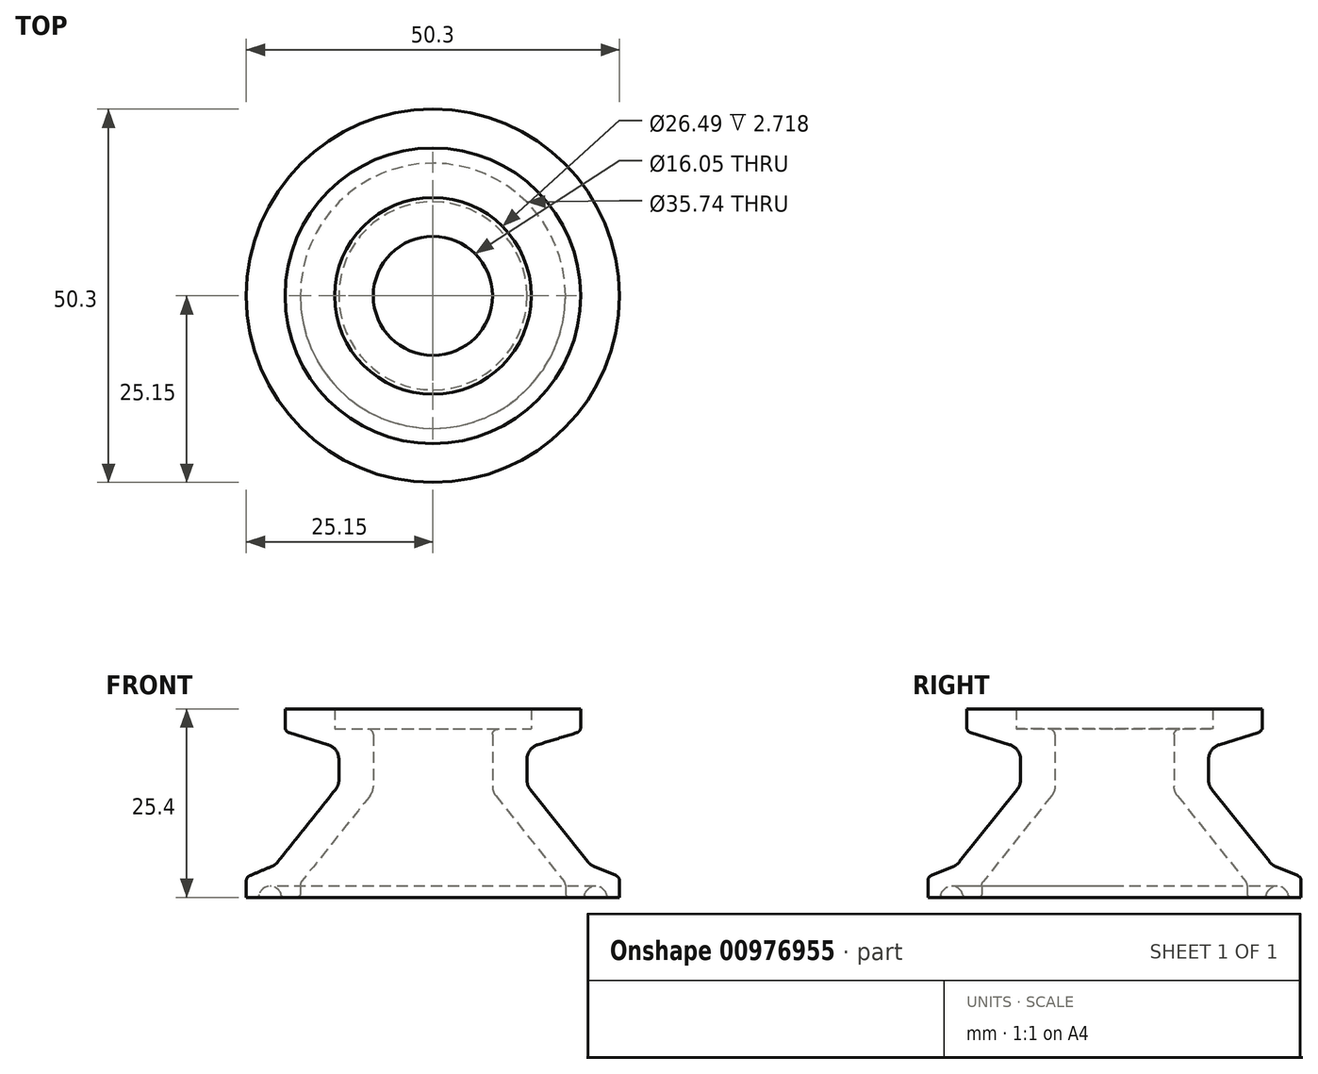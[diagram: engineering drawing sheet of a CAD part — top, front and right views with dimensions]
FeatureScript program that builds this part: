
annotation { "Feature Type Name" : "Feature", "Feature Type Description" : "" }
export const myFeature = defineFeature(function(context is Context, id is Id, definition is map)
    precondition{}
    {
        {
            var Q0;
            Q0=qCreatedBy(makeId("Front.planeOp"),FACE);
            var sketch = newSketch(context, id + "F0", { "sketchPlane" : qUnion([Q0])});
            skLineSegment(sketch, "E0", {"start": v(13.25, 6.14) * mm, "end": v(13.25, 8.85) * mm});
            skLineSegment(sketch, "E1", {"start": v(13.25, 8.85) * mm, "end": v(19.91, 8.85) * mm});
            skLineSegment(sketch, "E2", {"start": v(19.91, 8.85) * mm, "end": v(19.91, 5.8) * mm});
            skLineSegment(sketch, "E3", {"start": v(19.91, 5.8) * mm, "end": v(12.67, 3.57) * mm});
            skLineSegment(sketch, "E4", {"start": v(12.67, 3.57) * mm, "end": v(12.67, -1.46) * mm});
            skLineSegment(sketch, "E5", {"start": v(12.67, -1.46) * mm, "end": v(21.22, -12.18) * mm});
            skLineSegment(sketch, "E6", {"start": v(21.22, -12.18) * mm, "end": v(25.15, -13.8) * mm});
            skLineSegment(sketch, "E7", {"start": v(25.15, -13.8) * mm, "end": v(25.15, -16.55) * mm});
            skLineSegment(sketch, "E8", {"start": v(25.15, -16.55) * mm, "end": v(23.44, -16.55) * mm});
            skLineSegment(sketch, "E9", {"start": v(20.4, -16.55) * mm, "end": v(17.87, -16.55) * mm});
            skLineSegment(sketch, "E10", {"start": v(8.02, -1.46) * mm, "end": v(8.02, 6.14) * mm});
            skLineSegment(sketch, "E11", {"start": v(8.02, 6.14) * mm, "end": v(13.25, 6.14) * mm});
            skArc(sketch, "E12", {"start": v(23.44, -16.55) * mm, "mid": v(21.93, -15.03) * mm, "end": v(20.4, -16.55) * mm});
            skLineSegment(sketch, "E13", {"start": v(17.87, -16.55) * mm, "end": v(17.87, -14.63) * mm});
            skLineSegment(sketch, "E14", {"start": v(17.87, -14.63) * mm, "end": v(8.02, -2.28) * mm});
            skLineSegment(sketch, "E15", {"start": v(8.02, -2.28) * mm, "end": v(8.02, -1.46) * mm});
            skLineSegment(sketch, "E16", {"start": v(0, 0) * mm, "end": v(0, 35.98) * mm});
            skSolve(sketch);
        }
        {
            var Q0;
            Q0=makeQuery(id+"F0.imprint","IMPRINT",FACE,{"disambiguationData":[TD([[makeQuery(id+"F0.imprint","IMPRINT",EDGE,{"derivedFrom":sQuery(id+"F0.wireOp",EDGE,"E0")}),-1.0]])]});
            var Q1;
            Q1=sQuery(id+"F0.wireOp",EDGE,"E16");
            revolve(context, id + "F1", {"surfaceOperationType" : NewSurfaceOperationType.NEW, "entities" : qUnion([Q0]), "axis" : qUnion([Q1]), "revolveType" : RevolveType.FULL});
        }
        {
            var Q0;
            Q0=makeQuery(id+"F1.opRevolve","SWEPT_EDGE",EDGE,{"disambiguationData":[OSD([sQuery(id+"F0.wireOp",EDGE,"E6"),sQuery(id+"F0.wireOp",EDGE,"E7")])]});
            var Q1;
            Q1=makeQuery(id+"F1.opRevolve","SWEPT_EDGE",EDGE,{"disambiguationData":[OSD([sQuery(id+"F0.wireOp",EDGE,"E2"),sQuery(id+"F0.wireOp",EDGE,"E3")])]});
            var Q2;
            Q2=makeQuery(id+"F1.opRevolve","SWEPT_EDGE",EDGE,{"disambiguationData":[OSD([sQuery(id+"F0.wireOp",EDGE,"E10"),sQuery(id+"F0.wireOp",EDGE,"E11")])]});
            var Q3;
            Q3=makeQuery(id+"F1.opRevolve","SWEPT_EDGE",EDGE,{"disambiguationData":[OSD([sQuery(id+"F0.wireOp",EDGE,"E13"),sQuery(id+"F0.wireOp",EDGE,"E14")])]});
            fillet(context, id + "F2", {"entities" : qUnion([Q0, Q1, Q2, Q3]), "radius" : 0.76 * mm, "tangentPropagation" : true, "allowEdgeOverflow" : false});
        }
        {
            var Q0;
            Q0=makeQuery(id+"F1.opRevolve","SWEPT_EDGE",EDGE,{"disambiguationData":[OSD([sQuery(id+"F0.wireOp",EDGE,"E9"),sQuery(id+"F0.wireOp",EDGE,"E13")])]});
            fillet(context, id + "F3", {"entities" : qUnion([Q0]), "radius" : 0.5 * mm, "tangentPropagation" : true, "allowEdgeOverflow" : false});
        }
        {
            var Q0;
            Q0=makeQuery(id+"F1.opRevolve","SWEPT_EDGE",EDGE,{"disambiguationData":[OSD([sQuery(id+"F0.wireOp",EDGE,"E4"),sQuery(id+"F0.wireOp",EDGE,"E5")])]});
            var Q1;
            Q1=makeQuery(id+"F1.opRevolve","SWEPT_EDGE",EDGE,{"disambiguationData":[OSD([sQuery(id+"F0.wireOp",EDGE,"E3"),sQuery(id+"F0.wireOp",EDGE,"E4")])]});
            var Q2;
            Q2=makeQuery(id+"F1.opRevolve","SWEPT_EDGE",EDGE,{"disambiguationData":[OSD([sQuery(id+"F0.wireOp",EDGE,"E5"),sQuery(id+"F0.wireOp",EDGE,"E6")])]});
            var Q3;
            Q3=makeQuery(id+"F1.opRevolve","SWEPT_EDGE",EDGE,{"disambiguationData":[OSD([sQuery(id+"F0.wireOp",EDGE,"E14"),sQuery(id+"F0.wireOp",EDGE,"E15")])]});
            fillet(context, id + "F4", {"entities" : qUnion([Q0, Q1, Q2, Q3]), "radius" : 2.03 * mm, "tangentPropagation" : true, "allowEdgeOverflow" : false});
        }
        {
            var Q0;
            Q0=makeQuery(id+"F1.opRevolve","SWEPT_EDGE",EDGE,{"disambiguationData":[OSD([sQuery(id+"F0.wireOp",EDGE,"E8"),sQuery(id+"F0.wireOp",EDGE,"E12")])]});
            var Q1;
            Q1=makeQuery(id+"F1.opRevolve","SWEPT_EDGE",EDGE,{"disambiguationData":[OSD([sQuery(id+"F0.wireOp",EDGE,"E9"),sQuery(id+"F0.wireOp",EDGE,"E12")])]});
            fillet(context, id + "F5", {"entities" : qUnion([Q0, Q1]), "radius" : 0.38 * mm, "tangentPropagation" : true, "allowEdgeOverflow" : false});
        }
    });
